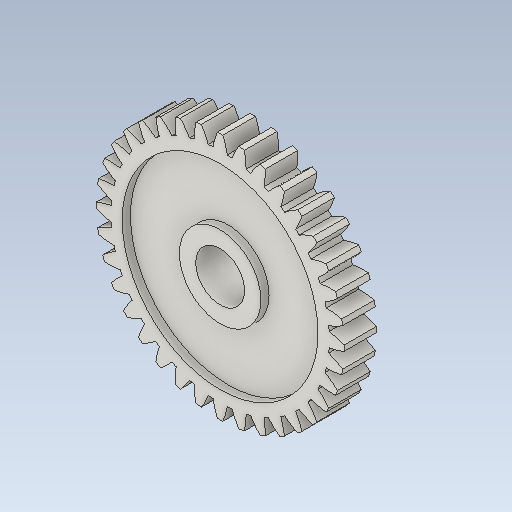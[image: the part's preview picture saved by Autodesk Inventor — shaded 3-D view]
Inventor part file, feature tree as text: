
AUTODESK INVENTOR PART (.ipt)
format: ipt  version: 2020.2 (Build 242310000, 310)  size: 306,688 bytes
history: imported  units: mm
features: imported_body x1
ambient origin geometry x8: Origin, YZ Plane, XZ Plane, XY Plane, X Axis, Y Axis, Z Axis, Center Point
bodies: Solide1 (imported_parasolid), Solid1 (imported_parasolid)
feature tree (1):
  imported_body  NMx_Import_Brep_tag  [imported B-rep: ~155 faces, bbox_mm=[30.392766, 30.392766, 8.8]]
